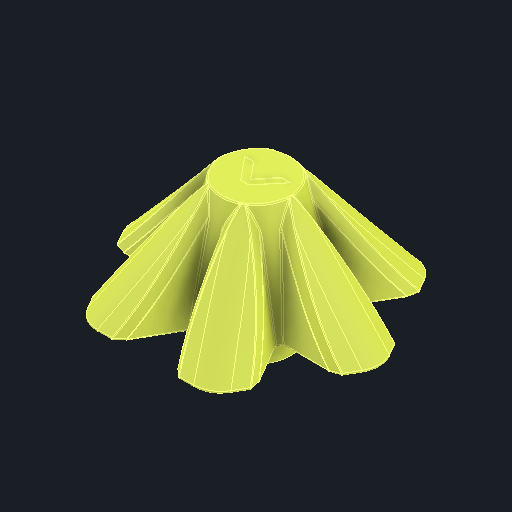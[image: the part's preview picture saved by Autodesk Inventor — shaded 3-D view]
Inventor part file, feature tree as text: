
AUTODESK INVENTOR PART (.ipt)
format: ipt  version: 2024.2 (Build 282272000, 272)  size: 3,515,904 bytes
history: native  units: in
note: dims shown in document units (in); Inventor stores cm internally (conversion verified against a paired STEP export)
features: fillet x1
ambient origin geometry x8: Origin, YZ Plane, XZ Plane, XY Plane, X Axis, Y Axis, Z Axis, Center Point
bodies: Solid1 (feature_tree)
feature tree (1):
  fillet  "Fillet156"  [1 undecoded]
note: 1 required parameter value undecoded (feature->parameter linkage not recoverable at this tier; creation-order binding heuristic only, values carry confidence <= 0.55)
